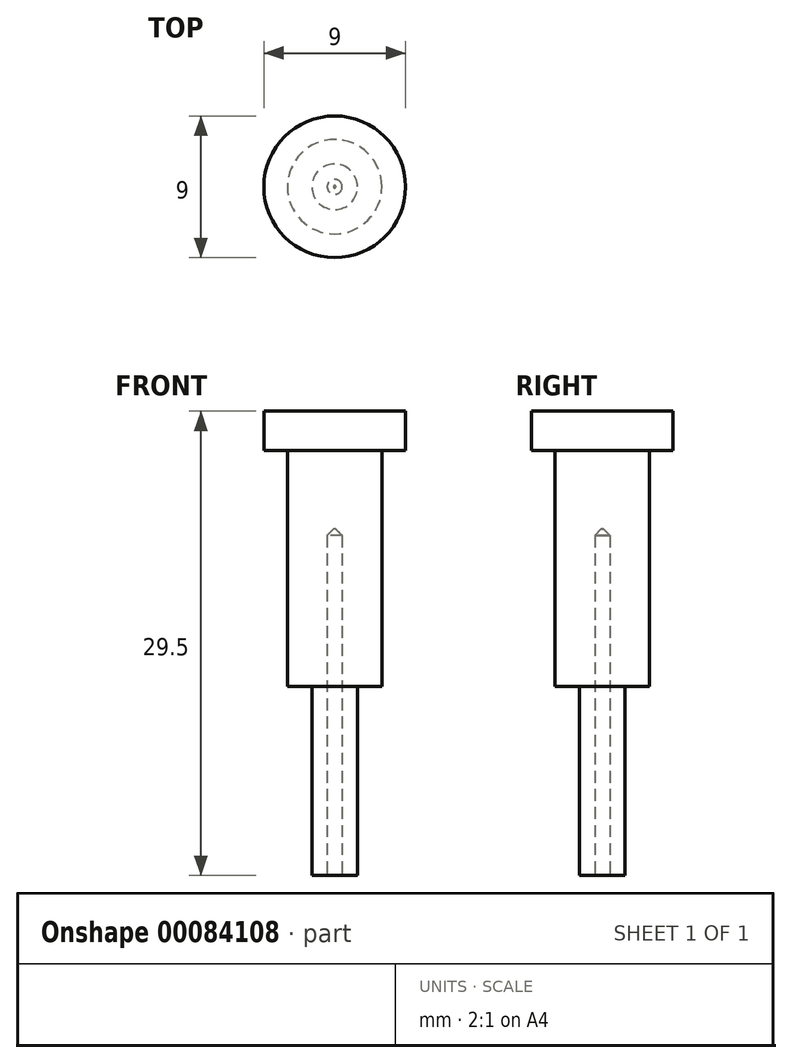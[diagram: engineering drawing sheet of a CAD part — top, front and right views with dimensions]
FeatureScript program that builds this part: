
annotation { "Feature Type Name" : "Feature", "Feature Type Description" : "" }
export const myFeature = defineFeature(function(context is Context, id is Id, definition is map)
    precondition{}
    {
        {
            var Q0;
            Q0=qCreatedBy(makeId("Top.planeOp"),FACE);
            var sketch = newSketch(context, id + "F0", { "sketchPlane" : qUnion([Q0])});
            skCircle(sketch, "E0", {"center": v(0, 0) * mm, "radius": 1.45 * mm});
            skSolve(sketch);
        }
        {
            var Q0;
            Q0 = qSketchRegion(id + "F0", true);
            extrude(context, id + "F1", {"entities" : qUnion([Q0]), "depth" : 12 * mm});
        }
        {
            var Q0;
            Q0=makeQuery(id+"F1.opExtrude","CAP_FACE",FACE,{"disambiguationData":[OSD([sQuery(id+"F0.wireOp",EDGE,"E0")])],"isStart":false});
            var sketch = newSketch(context, id + "F2", { "sketchPlane" : qUnion([Q0])});
            skCircle(sketch, "E1", {"center": v(0, 0) * mm, "radius": 3 * mm});
            skSolve(sketch);
        }
        {
            var Q0;
            Q0 = qSketchRegion(id + "F2", true);
            extrude(context, id + "F3", {"entities" : qUnion([Q0]), "operationType" : NewBodyOperationType.ADD, "depth" : 15 * mm});
        }
        {
            var Q0;
            Q0=makeQuery(id+"F3.opExtrude","CAP_FACE",FACE,{"disambiguationData":[OSD([sQuery(id+"F2.wireOp",EDGE,"E1")])],"isStart":false});
            var sketch = newSketch(context, id + "F4", { "sketchPlane" : qUnion([Q0])});
            skCircle(sketch, "E2", {"center": v(0, 0) * mm, "radius": 4.5 * mm});
            skSolve(sketch);
        }
        {
            var Q0;
            Q0 = qSketchRegion(id + "F4", true);
            extrude(context, id + "F5", {"entities" : qUnion([Q0]), "operationType" : NewBodyOperationType.ADD, "depth" : 2.5 * mm});
        }
        {
            var Q0;
            Q0=qCreatedBy(makeId("Top.planeOp"),FACE);
            var sketch = newSketch(context, id + "F6", { "sketchPlane" : qUnion([Q0])});
            skCircle(sketch, "E3", {"center": v(0, 0) * mm, "radius": 0.47 * mm});
            skSolve(sketch);
        }
        {
            var Q0;
            Q0 = qSketchRegion(id + "F6", true);
            extrude(context, id + "F7", {"entities" : qUnion([Q0]), "depth" : 22 * mm});
        }
        {
            var Q0;
            Q0=makeQuery(id+"F7.opExtrude","CAP_EDGE",EDGE,{"disambiguationData":[OSD([sQuery(id+"F6.wireOp",EDGE,"E3")])],"isStart":false});
            chamfer(context, id + "F8", {"entities" : qUnion([Q0]), "width" : 0.4 * mm, "tangentPropagation" : true});
        }
    });
